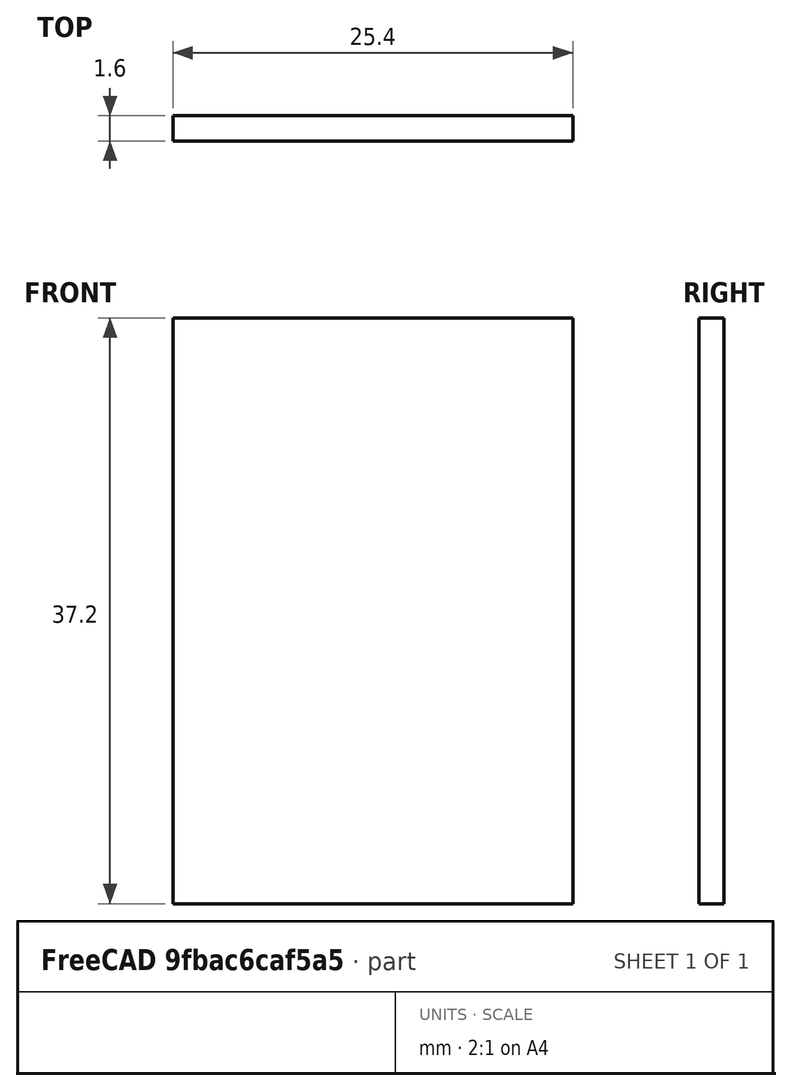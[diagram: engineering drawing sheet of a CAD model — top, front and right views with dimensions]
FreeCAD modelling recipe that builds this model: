
FCSTD DOCUMENT  (FreeCAD 0.20R29603 (Git))
Label: Right Throttle Board
License: All rights reserved
LicenseURL: http://en.wikipedia.org/wiki/All_rights_reserved
objects: Sketcher::SketchObject×1, PartDesign::Pad×1, PartDesign::Body×1
note: 4 computed .brp shape members not serialized (recipe doc carries the construction recipe); baked Part::Feature solids carry a one-line shape summary decoded from their .brp

FEATURE [Sketcher::SketchObject] Sketch001
  FullyConstrained = true
  MapMode = 5
  Placement = pos=(0,0,0) rot=(1,0,0;1.5708rad)
  Support = -> [XZ_Plane001]
  sketch-geometry (4):
    g0: LineSegment StartX=-12.7 StartY=18.6 StartZ=0 EndX=12.7 EndY=18.6 EndZ=0
    g1: LineSegment StartX=12.7 StartY=18.6 StartZ=0 EndX=12.7 EndY=-18.6 EndZ=0
    g2: LineSegment StartX=12.7 StartY=-18.6 StartZ=0 EndX=-12.7 EndY=-18.6 EndZ=0
    g3: LineSegment StartX=-12.7 StartY=-18.6 StartZ=0 EndX=-12.7 EndY=18.6 EndZ=0
  constraints (10):
    c: Coincident(g0,g1)
    c: Coincident(g1,g2)
    c: Coincident(g2,g3)
    c: Coincident(g3,g0)
    c: Horizontal(g0)
    c: Vertical(g1)
    c: Symmetric(g0,g2,g-1)
    c: Symmetric(g2,g1,g-2)
    c: DistanceX(g0,g0) = 25.4
    c: DistanceY(g1,g1) = 37.2
FEATURE [PartDesign::Pad] Pad
  Direction = (0,-1,2e-16)
  Length = 1.6
  Length2 = 10
  Placement = pos=(0,0,0) rot=(1,0,0;1.5708rad)
  Profile = -> Sketch001
  ReferenceAxis = -> Sketch001 [N_Axis]
  Type = 0
FEATURE [PartDesign::Body] Body001
  Group = -> [Sketch001,Pad]
  Origin = -> Origin001
  Tip = -> Pad
